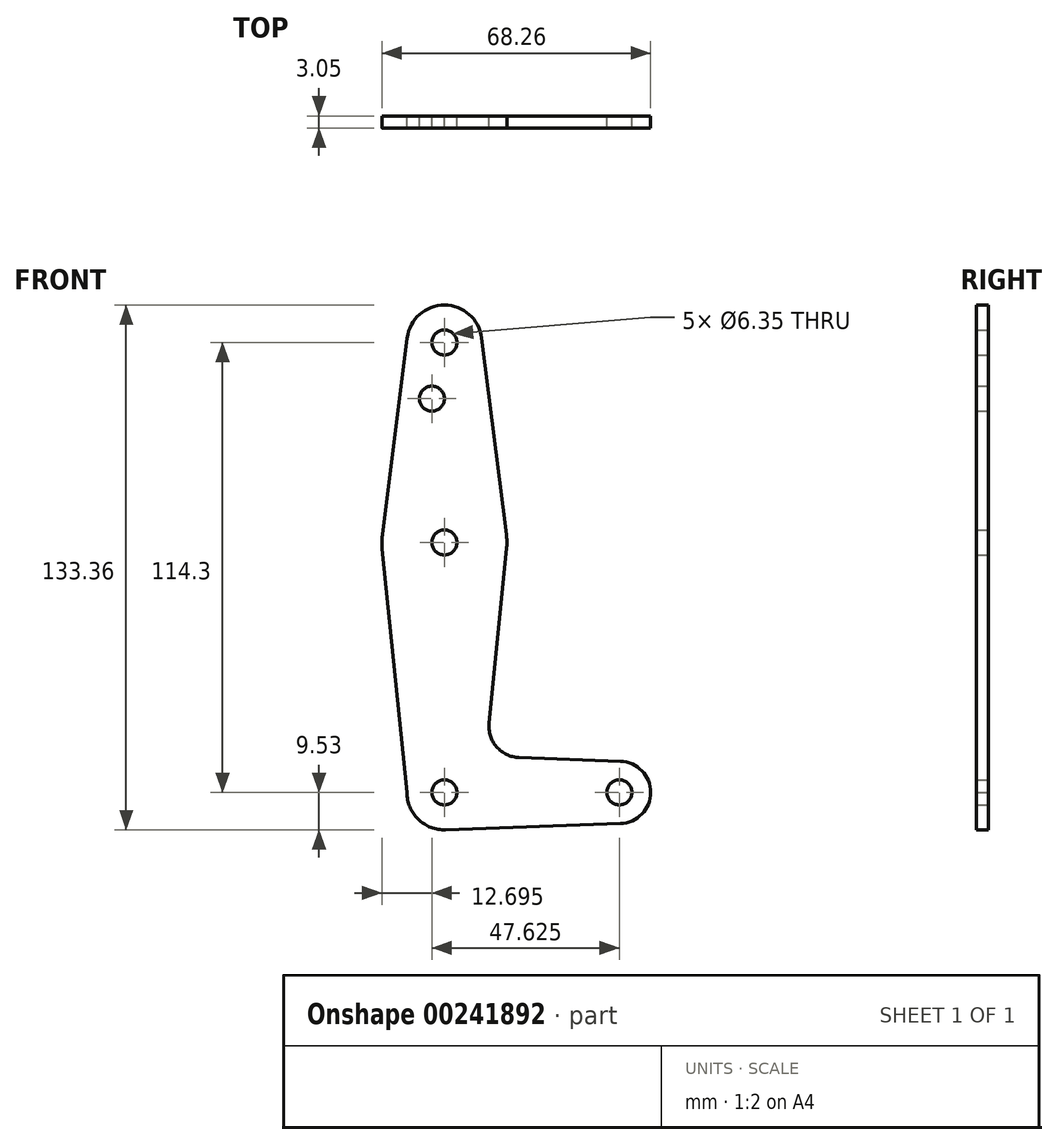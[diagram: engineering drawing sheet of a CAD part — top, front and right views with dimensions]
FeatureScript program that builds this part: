
annotation { "Feature Type Name" : "Feature", "Feature Type Description" : "" }
export const myFeature = defineFeature(function(context is Context, id is Id, definition is map)
    precondition{}
    {
        {
            var Q0;
            Q0=qCreatedBy(makeId("Front.planeOp"),FACE);
            var sketch = newSketch(context, id + "F0", { "sketchPlane" : qUnion([Q0])});
            skLineSegment(sketch, "E0", {"start": v(0, 0) * mm, "end": v(0, 114.3) * mm, "construction": true});
            skLineSegment(sketch, "E1", {"start": v(0, 0) * mm, "end": v(44.45, 0) * mm, "construction": true});
            skCircle(sketch, "E2", {"center": v(0, 114.3) * mm, "radius": 9.53 * mm});
            skCircle(sketch, "E3", {"center": v(0, 63.5) * mm, "radius": 15.88 * mm});
            skCircle(sketch, "E4", {"center": v(0, 0) * mm, "radius": 9.53 * mm});
            skCircle(sketch, "E5", {"center": v(44.45, 0) * mm, "radius": 7.94 * mm});
            skLineSegment(sketch, "E6", {"start": v(-9.45, 115.5) * mm, "end": v(-15.75, 65.48) * mm});
            skLineSegment(sketch, "E7", {"start": v(9.45, 115.5) * mm, "end": v(15.75, 65.48) * mm});
            skLineSegment(sketch, "E8", {"start": v(18.97, 8.85) * mm, "end": v(44.73, 7.93) * mm});
            skLineSegment(sketch, "E9", {"start": v(0.34, -9.52) * mm, "end": v(44.73, -7.93) * mm});
            skLineSegment(sketch, "E10", {"start": v(-9.53, 0) * mm, "end": v(-15.8, 61.9) * mm});
            skLineSegment(sketch, "E11", {"start": v(11.34, 17.6) * mm, "end": v(15.8, 61.91) * mm});
            skCircle(sketch, "E12", {"center": v(0, 114.3) * mm, "radius": 3.18 * mm});
            skCircle(sketch, "E13", {"center": v(0, 63.5) * mm, "radius": 3.18 * mm});
            skCircle(sketch, "E14", {"center": v(0, 0) * mm, "radius": 3.18 * mm});
            skCircle(sketch, "E15", {"center": v(44.45, 0) * mm, "radius": 3.18 * mm});
            skCircle(sketch, "E16", {"center": v(-3.17, 100.03) * mm, "radius": 3.18 * mm});
            skArc(sketch, "E17.filletArc", {"start": v(11.34, 17.6) * mm, "mid": v(13.26, 11.57) * mm, "end": v(18.97, 8.85) * mm});
            skSolve(sketch);
        }
        {
            var Q0;
            Q0 = qSketchRegion(id + "F0", true);
            extrude(context, id + "F1", {"entities" : qUnion([Q0]), "depth" : 3.05 * mm});
        }
    });
